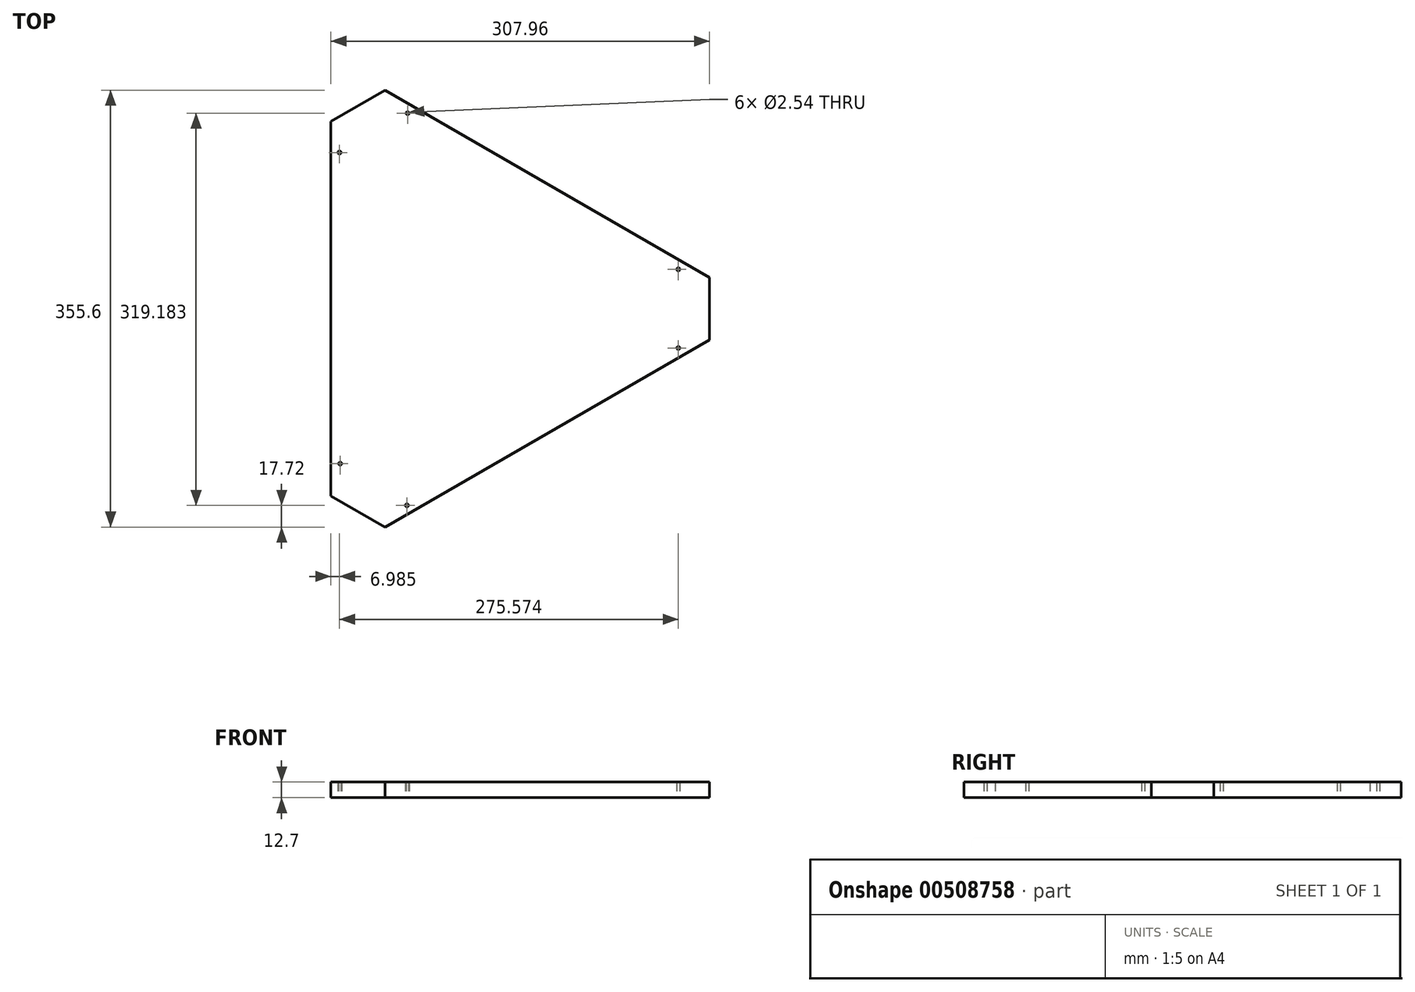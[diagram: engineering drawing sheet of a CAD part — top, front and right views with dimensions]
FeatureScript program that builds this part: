
annotation { "Feature Type Name" : "Feature", "Feature Type Description" : "" }
export const myFeature = defineFeature(function(context is Context, id is Id, definition is map)
    precondition{}
    {
        {
            var Q0;
            Q0=qCreatedBy(makeId("Top.planeOp"),FACE);
            var sketch = newSketch(context, id + "F0", { "sketchPlane" : qUnion([Q0])});
            skLineSegment(sketch, "E0.bottom", {"start": v(228.6, 228.6) * mm, "end": v(-228.6, 228.6) * mm, "construction": true});
            skLineSegment(sketch, "E0.top", {"start": v(228.6, -228.6) * mm, "end": v(-228.6, -228.6) * mm, "construction": true});
            skLineSegment(sketch, "E0.left", {"start": v(228.6, 228.6) * mm, "end": v(228.6, -228.6) * mm, "construction": true});
            skLineSegment(sketch, "E0.right", {"start": v(-228.6, 228.6) * mm, "end": v(-228.6, -228.6) * mm, "construction": true});
            skPoint(sketch, "E0.middle", {"position": v(0, 0) * mm});
            skCircle(sketch, "E1.cCircle", {"center": v(-29.1, 0) * mm, "radius": 234.64 * mm, "construction": true});
            skLineSegment(sketch, "E1.0", {"start": v(205.54, 0) * mm, "end": v(-146.4, -203.2) * mm, "construction": true});
            skLineSegment(sketch, "E1.1", {"start": v(-146.4, -203.2) * mm, "end": v(-146.4, 203.2) * mm, "construction": true});
            skLineSegment(sketch, "E1.2", {"start": v(-146.4, 203.2) * mm, "end": v(205.54, 0) * mm, "construction": true});
            skLineSegment(sketch, "E2", {"start": v(-146.4, -152.4) * mm, "end": v(-102.42, -177.8) * mm});
            skLineSegment(sketch, "E3", {"start": v(161.55, 25.4) * mm, "end": v(161.55, -25.4) * mm});
            skLineSegment(sketch, "E4", {"start": v(-146.4, 152.4) * mm, "end": v(-102.42, 177.8) * mm});
            skLineSegment(sketch, "E5", {"start": v(-146.4, 152.4) * mm, "end": v(-146.4, -152.4) * mm});
            skLineSegment(sketch, "E6", {"start": v(-102.42, -177.8) * mm, "end": v(161.55, -25.4) * mm});
            skLineSegment(sketch, "E7", {"start": v(161.55, 25.4) * mm, "end": v(-102.42, 177.8) * mm});
            skLineSegment(sketch, "E8", {"start": v(-124.41, 165.1) * mm, "end": v(-111.71, 143.1) * mm, "construction": true});
            skLineSegment(sketch, "E9", {"start": v(-139.43, 127.1) * mm, "end": v(-84, 159.1) * mm, "construction": true});
            skCircle(sketch, "E10", {"center": v(-139.43, 127.1) * mm, "radius": 1.27 * mm});
            skCircle(sketch, "E11", {"center": v(-84, 159.1) * mm, "radius": 1.27 * mm});
            skLineSegment(sketch, "E12", {"start": v(161.55, 0) * mm, "end": v(136.15, 0) * mm, "construction": true});
            skPoint(sketch, "E12.endSnap0", {"position": v(161.55, 0) * mm});
            skLineSegment(sketch, "E13", {"start": v(-124.41, -165.1) * mm, "end": v(-111.71, -143.1) * mm, "construction": true});
            skLineSegment(sketch, "E14", {"start": v(-138.84, -126.13) * mm, "end": v(-84.59, -160.08) * mm, "construction": true});
            skLineSegment(sketch, "E15", {"start": v(136.15, 32) * mm, "end": v(136.15, -32) * mm, "construction": true});
            skCircle(sketch, "E16", {"center": v(-138.84, -126.13) * mm, "radius": 1.27 * mm});
            skCircle(sketch, "E17", {"center": v(-84.59, -160.08) * mm, "radius": 1.27 * mm});
            skCircle(sketch, "E18", {"center": v(136.15, -32) * mm, "radius": 1.27 * mm});
            skCircle(sketch, "E19", {"center": v(136.15, 32) * mm, "radius": 1.27 * mm});
            skSolve(sketch);
        }
        {
            var Q0;
            Q0 = qSketchRegion(id + "F0", true);
            extrude(context, id + "F1", {"entities" : qUnion([Q0]), "depth" : 12.7 * mm});
        }
    });
